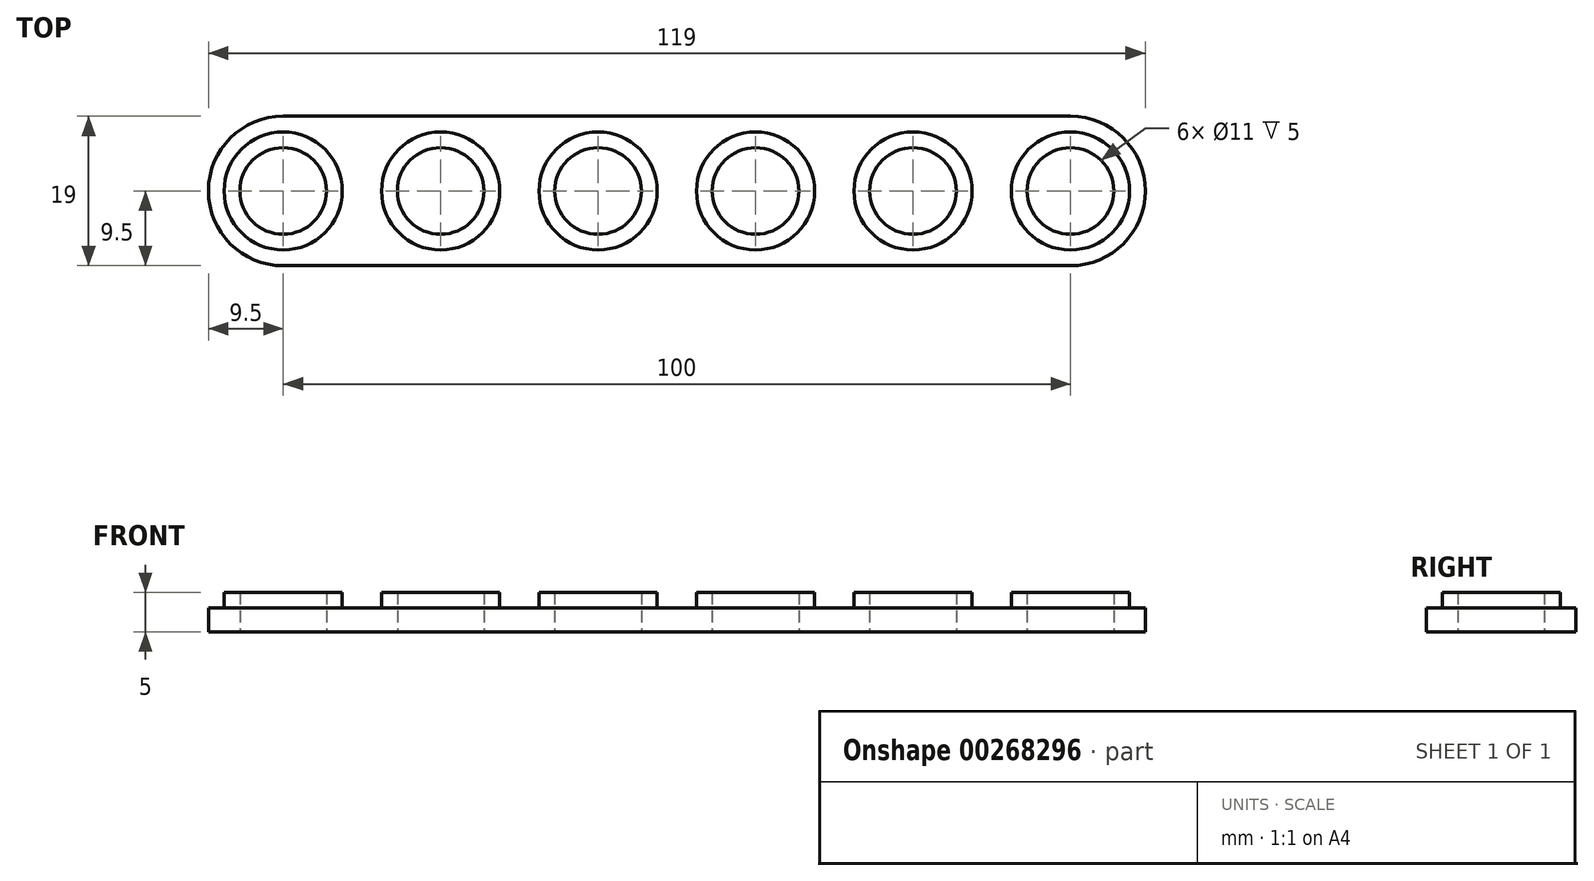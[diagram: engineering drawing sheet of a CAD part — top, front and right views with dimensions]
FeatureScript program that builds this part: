
annotation { "Feature Type Name" : "Feature", "Feature Type Description" : "" }
export const myFeature = defineFeature(function(context is Context, id is Id, definition is map)
    precondition{}
    {
        {
            var Q0;
            Q0=qCreatedBy(makeId("Top.planeOp"),FACE);
            var sketch = newSketch(context, id + "F0", { "sketchPlane" : qUnion([Q0])});
            skLineSegment(sketch, "E0.bottom", {"start": v(0, 9.5) * mm, "end": v(100, 9.5) * mm});
            skLineSegment(sketch, "E0.top", {"start": v(0, -9.5) * mm, "end": v(100, -9.5) * mm});
            skLineSegment(sketch, "E0.left", {"start": v(-9.5, 0) * mm, "end": v(-9.5, 0) * mm});
            skLineSegment(sketch, "E0.right", {"start": v(109.5, 0) * mm, "end": v(109.5, 0) * mm});
            skPoint(sketch, "E1", {"position": v(-9.5, 0) * mm});
            skCircle(sketch, "E2", {"center": v(0, 0) * mm, "radius": 5.5 * mm});
            skPoint(sketch, "E3.visualSharp", {"position": v(109.5, 9.5) * mm});
            skArc(sketch, "E3.filletArc", {"start": v(109.5, 0) * mm, "mid": v(106.72, 6.72) * mm, "end": v(100, 9.5) * mm});
            skPoint(sketch, "E4.visualSharp", {"position": v(109.5, -9.5) * mm});
            skArc(sketch, "E4.filletArc", {"start": v(100, -9.5) * mm, "mid": v(106.72, -6.72) * mm, "end": v(109.5, 0) * mm});
            skPoint(sketch, "E5.visualSharp", {"position": v(-9.5, -9.5) * mm});
            skArc(sketch, "E5.filletArc", {"start": v(-9.5, 0) * mm, "mid": v(-6.72, -6.72) * mm, "end": v(0, -9.5) * mm});
            skPoint(sketch, "E6.visualSharp", {"position": v(-9.5, 9.5) * mm});
            skArc(sketch, "E6.filletArc", {"start": v(0, 9.5) * mm, "mid": v(-6.72, 6.72) * mm, "end": v(-9.5, 0) * mm});
            skCircle(sketch, "E7", {"center": v(0, 0) * mm, "radius": 7.5 * mm});
            skCircle(sketch, "E8.1.0.0", {"center": v(20, 0) * mm, "radius": 5.5 * mm});
            skCircle(sketch, "E8.1.0.1", {"center": v(20, 0) * mm, "radius": 7.5 * mm});
            skCircle(sketch, "E8.2.0.0", {"center": v(40, 0) * mm, "radius": 5.5 * mm});
            skCircle(sketch, "E8.2.0.1", {"center": v(40, 0) * mm, "radius": 7.5 * mm});
            skCircle(sketch, "E8.3.0.0", {"center": v(60, 0) * mm, "radius": 5.5 * mm});
            skCircle(sketch, "E8.3.0.1", {"center": v(60, 0) * mm, "radius": 7.5 * mm});
            skCircle(sketch, "E8.4.0.0", {"center": v(80, 0) * mm, "radius": 5.5 * mm});
            skCircle(sketch, "E8.4.0.1", {"center": v(80, 0) * mm, "radius": 7.5 * mm});
            skLineSegment(sketch, "E8.direction1", {"start": v(0, 0) * mm, "end": v(20, 0) * mm, "construction": true});
            skCircle(sketch, "E9.0.5.0", {"center": v(100, 0) * mm, "radius": 5.5 * mm});
            skCircle(sketch, "E9.2.5.0", {"center": v(100, 0) * mm, "radius": 7.5 * mm});
            skSolve(sketch);
        }
        {
            var Q0;
            Q0=qSketchRegion(id+"F0",true);
            extrude(context, id + "F1", {"entities" : qUnion([Q0]), "depth" : 3 * mm});
        }
        {
            var Q0;
            Q0=makeQuery(id+"F0.imprint","IMPRINT",FACE,{"disambiguationData":[TD([[makeQuery(id+"F0.imprint","IMPRINT",EDGE,{"derivedFrom":sQuery(id+"F0.wireOp",EDGE,"E2")}),-1.0]])]});
            var Q1;
            Q1=makeQuery(id+"F0.imprint","IMPRINT",FACE,{"disambiguationData":[TD([[makeQuery(id+"F0.imprint","IMPRINT",EDGE,{"derivedFrom":sQuery(id+"F0.wireOp",EDGE,"E8.1.0.0")}),-1.0]])]});
            var Q2;
            Q2=makeQuery(id+"F0.imprint","IMPRINT",FACE,{"disambiguationData":[TD([[makeQuery(id+"F0.imprint","IMPRINT",EDGE,{"derivedFrom":sQuery(id+"F0.wireOp",EDGE,"E8.2.0.0")}),-1.0]])]});
            var Q3;
            Q3=makeQuery(id+"F0.imprint","IMPRINT",FACE,{"disambiguationData":[TD([[makeQuery(id+"F0.imprint","IMPRINT",EDGE,{"derivedFrom":sQuery(id+"F0.wireOp",EDGE,"E8.3.0.0")}),-1.0]])]});
            var Q4;
            Q4=makeQuery(id+"F0.imprint","IMPRINT",FACE,{"disambiguationData":[TD([[makeQuery(id+"F0.imprint","IMPRINT",EDGE,{"derivedFrom":sQuery(id+"F0.wireOp",EDGE,"E8.4.0.0")}),-1.0]])]});
            var Q5;
            Q5=makeQuery(id+"F0.imprint","IMPRINT",FACE,{"disambiguationData":[TD([[makeQuery(id+"F0.imprint","IMPRINT",EDGE,{"derivedFrom":sQuery(id+"F0.wireOp",EDGE,"E9.0.5.0")}),-1.0]])]});
            extrude(context, id + "F2", {"entities" : qUnion([Q0, Q1, Q2, Q3, Q4, Q5]), "operationType" : NewBodyOperationType.ADD, "depth" : 5 * mm});
        }
        {
            var Q0;
            Q0=makeQuery(id+"F1.opExtrude","SWEPT_BODY",BODY,{"disambiguationData":[OSD([sQuery(id+"F0.wireOp",EDGE,"E0.bottom"),sQuery(id+"F0.wireOp",EDGE,"E0.top"),sQuery(id+"F0.wireOp",EDGE,"E3.filletArc"),sQuery(id+"F0.wireOp",EDGE,"E4.filletArc"),sQuery(id+"F0.wireOp",EDGE,"E5.filletArc"),sQuery(id+"F0.wireOp",EDGE,"E6.filletArc"),sQuery(id+"F0.wireOp",EDGE,"E7"),sQuery(id+"F0.wireOp",EDGE,"E8.1.0.1"),sQuery(id+"F0.wireOp",EDGE,"E8.2.0.1"),sQuery(id+"F0.wireOp",EDGE,"E8.3.0.1"),sQuery(id+"F0.wireOp",EDGE,"E8.4.0.1")])]});
            var Q1;
            Q1=makeQuery(id+"F2.opExtrude","SWEPT_FACE",FACE,{"disambiguationData":[OSD([sQuery(id+"F0.wireOp",EDGE,"E2")])]});
            transform(context, id + "F3", {"entities" : qUnion([Q0]), "transformType" : TransformType.ROTATION, "transformAxis" : qUnion([Q1]), "angle" : 270 * degree, "makeCopy" : true});
        }
        {
            var Q0;
            Q0=makeQuery(id+"F3.opPattern","COPY",BODY,{"derivedFrom":makeQuery(id+"F1.opExtrude","SWEPT_BODY",BODY,{"disambiguationData":[OSD([sQuery(id+"F0.wireOp",EDGE,"E0.bottom"),sQuery(id+"F0.wireOp",EDGE,"E0.top"),sQuery(id+"F0.wireOp",EDGE,"E3.filletArc"),sQuery(id+"F0.wireOp",EDGE,"E4.filletArc"),sQuery(id+"F0.wireOp",EDGE,"E5.filletArc"),sQuery(id+"F0.wireOp",EDGE,"E6.filletArc"),sQuery(id+"F0.wireOp",EDGE,"E7"),sQuery(id+"F0.wireOp",EDGE,"E8.1.0.1"),sQuery(id+"F0.wireOp",EDGE,"E8.2.0.1"),sQuery(id+"F0.wireOp",EDGE,"E8.3.0.1"),sQuery(id+"F0.wireOp",EDGE,"E8.4.0.1")])]}),"instanceName":"1"});
            transform(context, id + "F4", {"entities" : qUnion([Q0]), "transformType" : TransformType.TRANSLATION_3D, "dx" : 20 * mm, "dy" : 0 * mm, "dz" : 0 * mm, "makeCopy" : false});
        }
        {
            var Q0;
            Q0=makeQuery(id+"F3.opPattern","COPY",BODY,{"derivedFrom":makeQuery(id+"F1.opExtrude","SWEPT_BODY",BODY,{"disambiguationData":[OSD([sQuery(id+"F0.wireOp",EDGE,"E0.bottom"),sQuery(id+"F0.wireOp",EDGE,"E0.top"),sQuery(id+"F0.wireOp",EDGE,"E3.filletArc"),sQuery(id+"F0.wireOp",EDGE,"E4.filletArc"),sQuery(id+"F0.wireOp",EDGE,"E5.filletArc"),sQuery(id+"F0.wireOp",EDGE,"E6.filletArc"),sQuery(id+"F0.wireOp",EDGE,"E7"),sQuery(id+"F0.wireOp",EDGE,"E8.1.0.1"),sQuery(id+"F0.wireOp",EDGE,"E8.2.0.1"),sQuery(id+"F0.wireOp",EDGE,"E8.3.0.1"),sQuery(id+"F0.wireOp",EDGE,"E8.4.0.1")])]}),"instanceName":"1"});
            deleteBodies(context, id + "F5", {"entities" : qUnion([Q0])});
        }
    });
